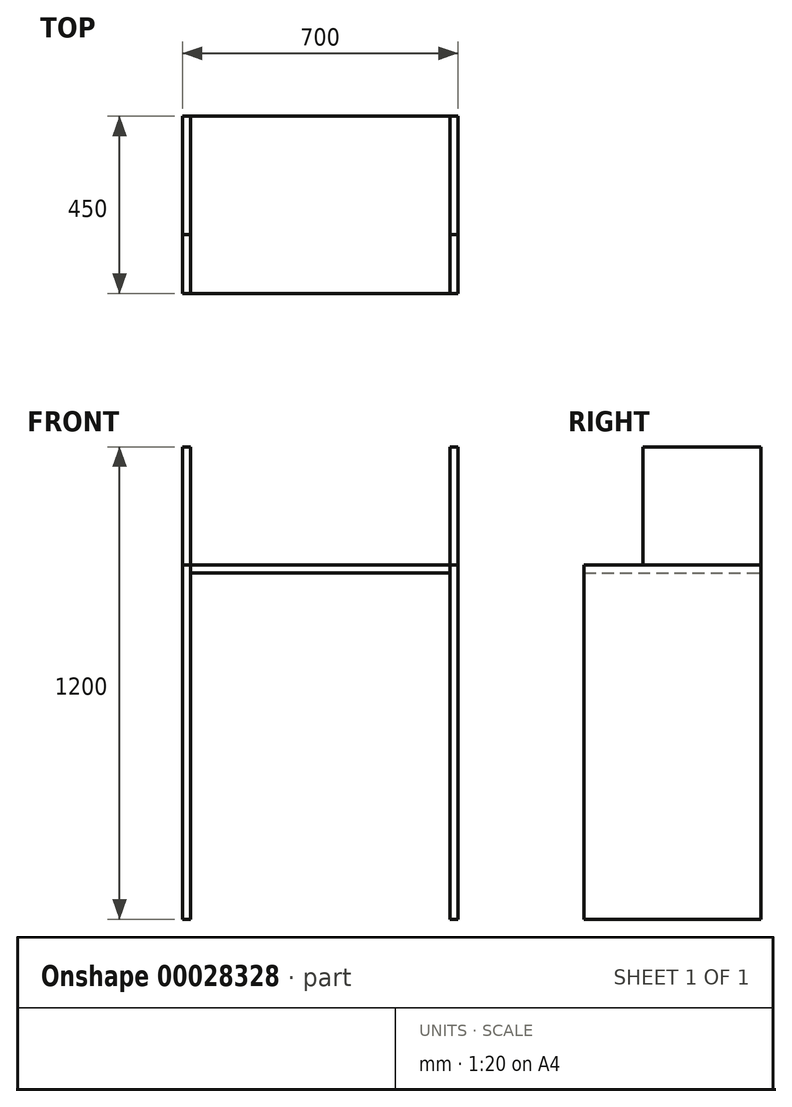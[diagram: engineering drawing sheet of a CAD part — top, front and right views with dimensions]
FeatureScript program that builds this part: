
annotation { "Feature Type Name" : "Feature", "Feature Type Description" : "" }
export const myFeature = defineFeature(function(context is Context, id is Id, definition is map)
    precondition{}
    {
        {
            var Q0;
            Q0=qCreatedBy(makeId("Top.planeOp"),FACE);
            var sketch = newSketch(context, id + "F0", { "sketchPlane" : qUnion([Q0])});
            skLineSegment(sketch, "E0.bottom", {"start": v(-294.4, 225.48) * mm, "end": v(-274.4, 225.48) * mm});
            skLineSegment(sketch, "E0.top", {"start": v(-294.4, -224.52) * mm, "end": v(-274.4, -224.52) * mm});
            skLineSegment(sketch, "E0.left", {"start": v(-294.4, 225.48) * mm, "end": v(-294.4, -224.52) * mm});
            skLineSegment(sketch, "E0.right", {"start": v(-274.4, 225.48) * mm, "end": v(-274.4, -224.52) * mm});
            skLineSegment(sketch, "E1.left", {"start": v(385.6, 225.48) * mm, "end": v(385.6, -224.52) * mm});
            skLineSegment(sketch, "E1.right", {"start": v(405.6, 225.48) * mm, "end": v(405.6, -224.52) * mm});
            skLineSegment(sketch, "E1.top", {"start": v(385.6, -224.52) * mm, "end": v(405.6, -224.52) * mm});
            skLineSegment(sketch, "E1.bottom", {"start": v(385.6, 225.48) * mm, "end": v(405.6, 225.48) * mm});
            skSolve(sketch);
        }
        {
            var Q0;
            Q0 = qSketchRegion(id + "F0", true);
            extrude(context, id + "F1", {"entities" : qUnion([Q0]), "depth" : 900 * mm});
        }
        {
            var Q0;
            Q0=makeQuery(id+"F1.opExtrude","SWEPT_FACE",FACE,{"disambiguationData":[OSD([sQuery(id+"F0.wireOp",EDGE,"E0.right")])]});
            var sketch = newSketch(context, id + "F2", { "sketchPlane" : qUnion([Q0])});
            skLineSegment(sketch, "E2.bottom", {"start": v(-224.52, 900) * mm, "end": v(225.48, 900) * mm});
            skLineSegment(sketch, "E2.top", {"start": v(-224.52, 880) * mm, "end": v(225.48, 880) * mm});
            skLineSegment(sketch, "E2.left", {"start": v(-224.52, 900) * mm, "end": v(-224.52, 880) * mm});
            skLineSegment(sketch, "E2.right", {"start": v(225.48, 900) * mm, "end": v(225.48, 880) * mm});
            skSolve(sketch);
        }
        {
            var Q0;
            Q0 = qSketchRegion(id + "F2", true);
            var Q1;
            Q1=makeQuery(id+"F1.opExtrude","SWEPT_FACE",FACE,{"disambiguationData":[OSD([sQuery(id+"F0.wireOp",EDGE,"E1.left")])]});
            extrude(context, id + "F3", {"entities" : qUnion([Q0]), "endBound" : BoundingType.UP_TO_SURFACE, "endBoundEntityFace" : qUnion([Q1]), "depth" : 25 * mm});
        }
        {
            var Q0;
            Q0=makeQuery(id+"F3.opExtrude","SWEPT_FACE",FACE,{"disambiguationData":[OSD([sQuery(id+"F2.wireOp",EDGE,"E2.bottom")])]});
            var sketch = newSketch(context, id + "F4", { "sketchPlane" : qUnion([Q0])});
            skLineSegment(sketch, "E3.bottom", {"start": v(-274.4, 225.48) * mm, "end": v(-294.4, 225.48) * mm});
            skLineSegment(sketch, "E3.top", {"start": v(-274.4, -74.52) * mm, "end": v(-294.4, -74.52) * mm});
            skLineSegment(sketch, "E3.left", {"start": v(-274.4, 225.48) * mm, "end": v(-274.4, -74.52) * mm});
            skLineSegment(sketch, "E3.right", {"start": v(-294.4, 225.48) * mm, "end": v(-294.4, -74.52) * mm});
            skLineSegment(sketch, "E4.bottom", {"start": v(385.6, 225.48) * mm, "end": v(405.6, 225.48) * mm});
            skLineSegment(sketch, "E4.top", {"start": v(385.6, -74.52) * mm, "end": v(405.6, -74.52) * mm});
            skLineSegment(sketch, "E4.left", {"start": v(385.6, 225.48) * mm, "end": v(385.6, -74.52) * mm});
            skLineSegment(sketch, "E4.right", {"start": v(405.6, 225.48) * mm, "end": v(405.6, -74.52) * mm});
            skSolve(sketch);
        }
        {
            var Q0;
            Q0 = qSketchRegion(id + "F4", true);
            extrude(context, id + "F5", {"entities" : qUnion([Q0]), "depth" : 300 * mm});
        }
    });
